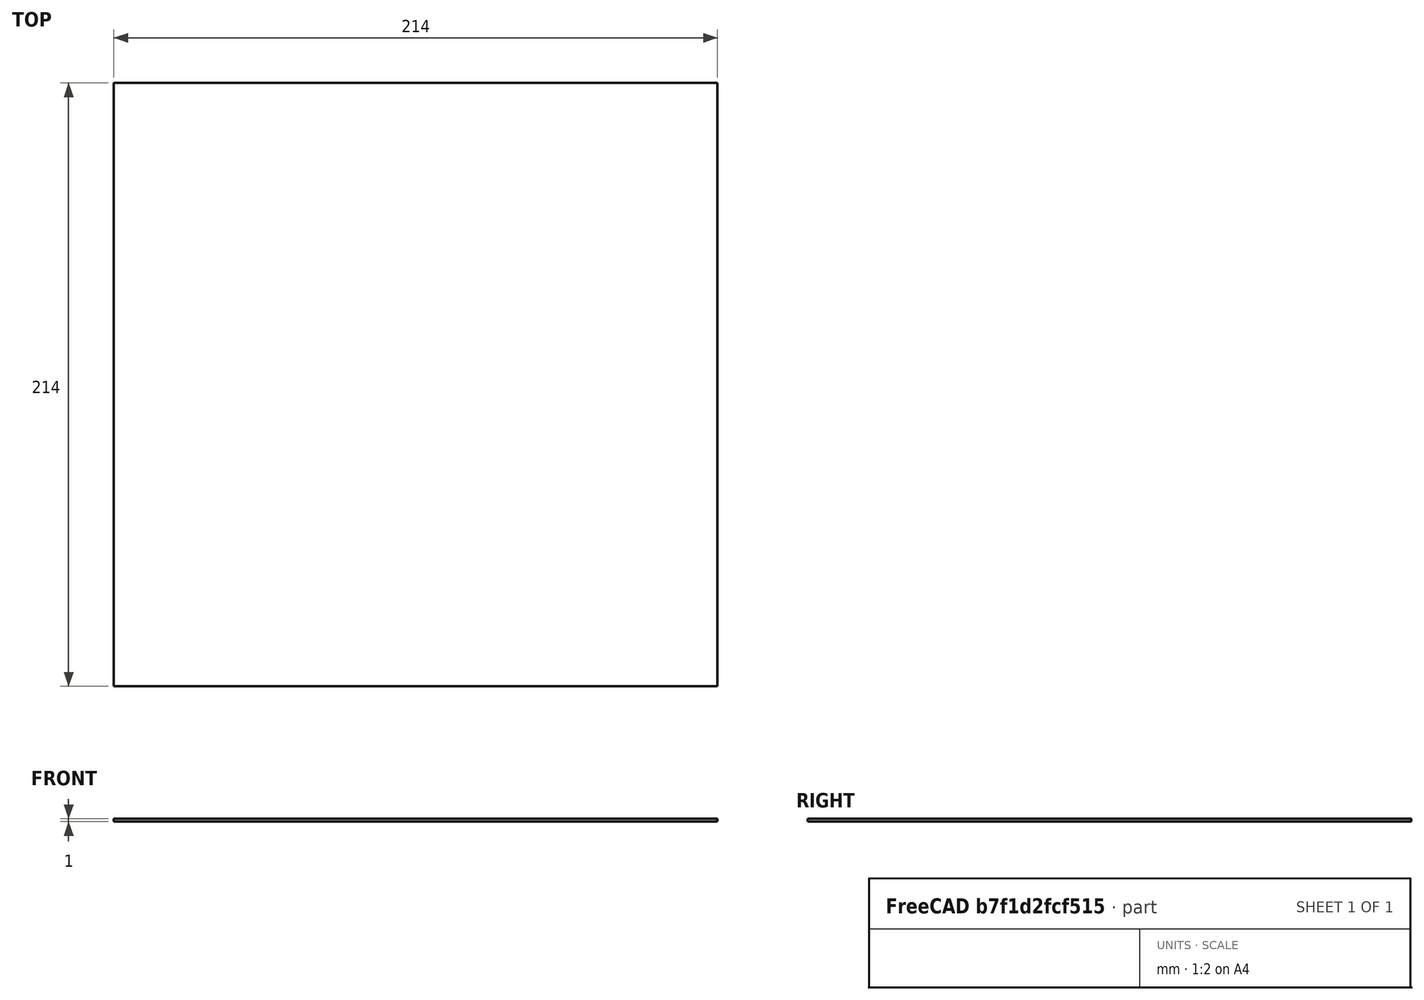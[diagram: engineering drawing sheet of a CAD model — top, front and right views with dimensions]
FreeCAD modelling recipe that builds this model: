
FCSTD DOCUMENT  (FreeCAD 0.17R13519 (Git))
Label: Heatbed_carpet_214x214x3mm
License: All rights reserved
LicenseURL: http://en.wikipedia.org/wiki/All_rights_reserved
objects: Sketcher::SketchObject×1, PartDesign::Pad×1, PartDesign::Body×1
note: 4 computed .brp shape members not serialized (recipe doc carries the construction recipe); baked Part::Feature solids carry a one-line shape summary decoded from their .brp

FEATURE [Sketcher::SketchObject] Sketch
  MapMode = 5
  Support = -> [XY_Plane]
  sketch-geometry (4):
    g0: LineSegment StartX=-107 StartY=107 StartZ=0 EndX=107 EndY=107 EndZ=0
    g1: LineSegment StartX=107 StartY=107 StartZ=0 EndX=107 EndY=-107 EndZ=0
    g2: LineSegment StartX=107 StartY=-107 StartZ=0 EndX=-107 EndY=-107 EndZ=0
    g3: LineSegment StartX=-107 StartY=-107 StartZ=0 EndX=-107 EndY=107 EndZ=0
  constraints (12):
    c: Coincident(g0,g1)
    c: Coincident(g1,g2)
    c: Coincident(g2,g3)
    c: Coincident(g3,g0)
    c: Horizontal(g0)
    c: Horizontal(g2)
    c: Vertical(g1)
    c: Vertical(g3)
    c: Symmetric(g0,g0,g-2)
    c: Symmetric(g0,g2,g-1)
    c: Equal(g0,g3)
    c: DistanceY(g3,g3) = 214
FEATURE [PartDesign::Pad] Pad
  Length = 1
  Length2 = 100
  Profile = -> Sketch
  Type = 0
FEATURE [PartDesign::Body] Body
  Group = -> [Sketch,Pad]
  Origin = -> Origin
  Tip = -> Pad
